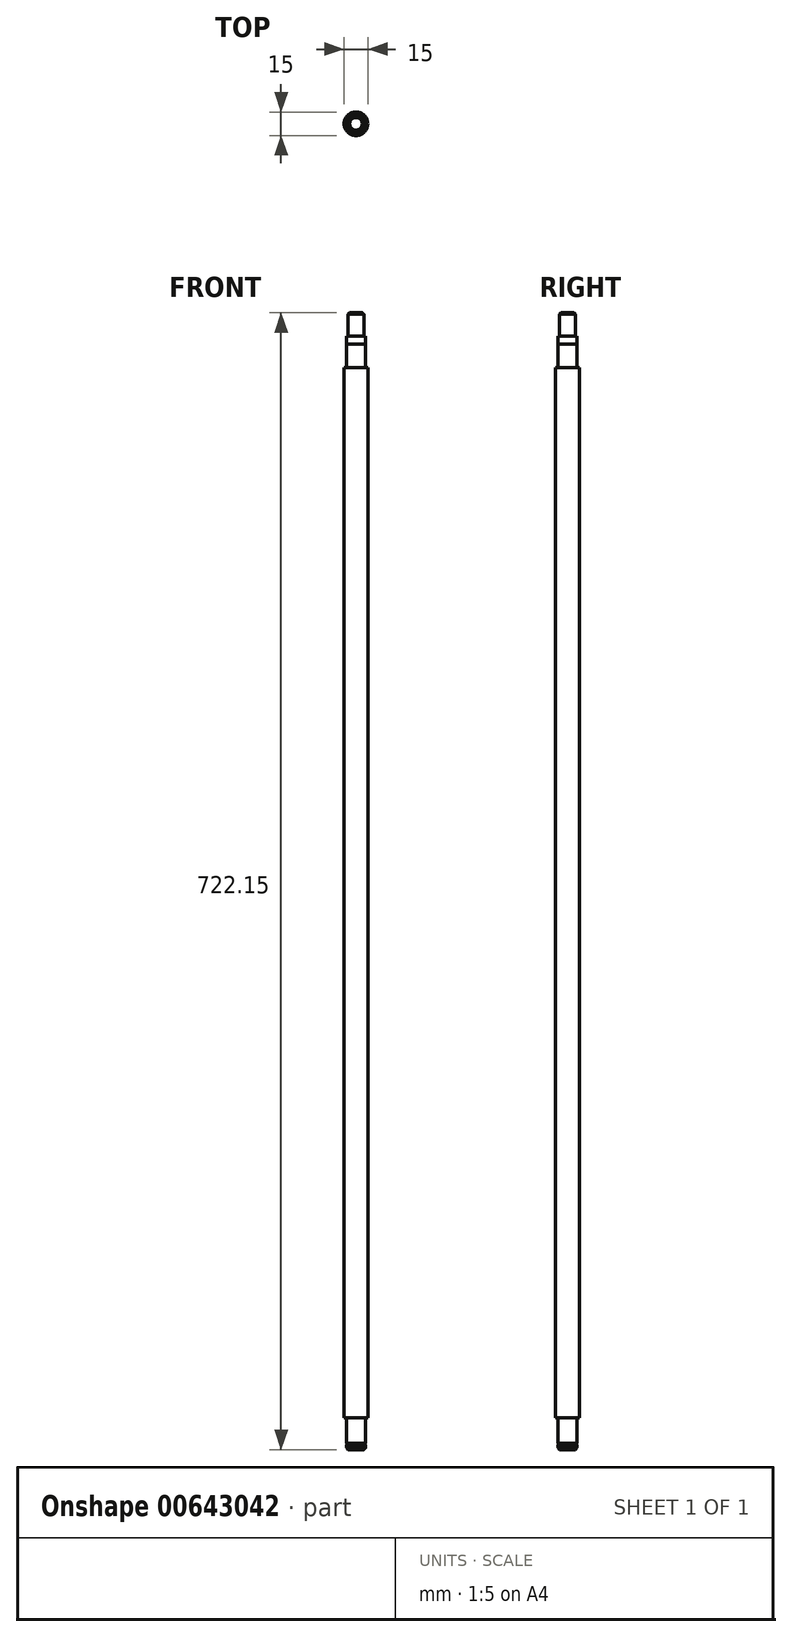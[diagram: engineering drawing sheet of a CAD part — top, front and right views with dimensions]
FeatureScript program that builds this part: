
annotation { "Feature Type Name" : "Feature", "Feature Type Description" : "" }
export const myFeature = defineFeature(function(context is Context, id is Id, definition is map)
    precondition{}
    {
        {
            var Q0;
            Q0=qCreatedBy(makeId("Top.planeOp"),FACE);
            var sketch = newSketch(context, id + "F0", { "sketchPlane" : qUnion([Q0])});
            skCircle(sketch, "E0", {"center": v(0, 0) * mm, "radius": 6 * mm});
            skSolve(sketch);
        }
        {
            var Q0;
            Q0=makeQuery(id+"F0.imprint","IMPRINT",FACE,{"disambiguationData":[TD([[makeQuery(id+"F0.imprint","IMPRINT",EDGE,{"derivedFrom":sQuery(id+"F0.wireOp",EDGE,"E0")}),1.0]])]});
            extrude(context, id + "F1", {"entities" : qUnion([Q0]), "depth" : 3 * mm});
        }
        {
            var Q0;
            Q0=makeQuery(id+"F1.opExtrude","CAP_FACE",FACE,{"disambiguationData":[OSD([sQuery(id+"F0.wireOp",EDGE,"E0")])],"isStart":false});
            var sketch = newSketch(context, id + "F2", { "sketchPlane" : qUnion([Q0])});
            skCircle(sketch, "E1", {"center": v(0, 0) * mm, "radius": 5.75 * mm});
            skSolve(sketch);
        }
        {
            var Q0;
            Q0=makeQuery(id+"F2.imprint","IMPRINT",FACE,{"disambiguationData":[TD([[makeQuery(id+"F2.imprint","IMPRINT",EDGE,{"derivedFrom":sQuery(id+"F2.wireOp",EDGE,"E1")}),1.0]])]});
            extrude(context, id + "F3", {"entities" : qUnion([Q0]), "operationType" : NewBodyOperationType.ADD, "depth" : 1.15 * mm});
        }
        {
            var Q0;
            Q0=makeQuery(id+"F3.opExtrude","CAP_FACE",FACE,{"disambiguationData":[OSD([sQuery(id+"F2.wireOp",EDGE,"E1")])],"isStart":false});
            var sketch = newSketch(context, id + "F4", { "sketchPlane" : qUnion([Q0])});
            skCircle(sketch, "E2", {"center": v(0, 0) * mm, "radius": 6 * mm});
            skSolve(sketch);
        }
        {
            var Q0;
            Q0=makeQuery(id+"F4.imprint","IMPRINT",FACE,{"disambiguationData":[TD([[makeQuery(id+"F4.imprint","IMPRINT",EDGE,{"derivedFrom":sQuery(id+"F4.wireOp",EDGE,"E2")}),1.0]])]});
            var Q1;
            Q1=makeQuery(id+"F4.imprint","IMPRINT",FACE,{"disambiguationData":[TD([[makeQuery(id+"F4.imprint","IMPRINT",EDGE,{"derivedFrom":makeQuery(id+"F3.opExtrude","CAP_EDGE",EDGE,{"disambiguationData":[OSD([sQuery(id+"F2.wireOp",EDGE,"E1")])],"isStart":false})}),1.0]])]});
            extrude(context, id + "F5", {"entities" : qUnion([Q0, Q1]), "operationType" : NewBodyOperationType.ADD, "depth" : 16 * mm});
        }
        {
            var Q0;
            Q0=makeQuery(id+"F5.opExtrude","CAP_FACE",FACE,{"disambiguationData":[OSD([sQuery(id+"F4.wireOp",EDGE,"E2")])],"isStart":false});
            var sketch = newSketch(context, id + "F6", { "sketchPlane" : qUnion([Q0])});
            skCircle(sketch, "E3", {"center": v(0, 0) * mm, "radius": 7.5 * mm});
            skSolve(sketch);
        }
        {
            var Q0;
            Q0=makeQuery(id+"F6.imprint","IMPRINT",FACE,{"disambiguationData":[TD([[makeQuery(id+"F6.imprint","IMPRINT",EDGE,{"derivedFrom":makeQuery(id+"F5.opExtrude","CAP_EDGE",EDGE,{"disambiguationData":[OSD([sQuery(id+"F4.wireOp",EDGE,"E2")])],"isStart":false})}),1.0]])]});
            var Q1;
            Q1=makeQuery(id+"F6.imprint","IMPRINT",FACE,{"disambiguationData":[TD([[makeQuery(id+"F6.imprint","IMPRINT",EDGE,{"derivedFrom":sQuery(id+"F6.wireOp",EDGE,"E3")}),1.0]])]});
            extrude(context, id + "F7", {"entities" : qUnion([Q0, Q1]), "operationType" : NewBodyOperationType.ADD, "depth" : 667 * mm});
        }
        {
            var Q0;
            Q0=makeQuery(id+"F7.opExtrude","CAP_FACE",FACE,{"disambiguationData":[OSD([sQuery(id+"F6.wireOp",EDGE,"E3")])],"isStart":false});
            var sketch = newSketch(context, id + "F8", { "sketchPlane" : qUnion([Q0])});
            skCircle(sketch, "E4", {"center": v(0, 0) * mm, "radius": 6 * mm});
            skSolve(sketch);
        }
        {
            var Q0;
            Q0=makeQuery(id+"F8.imprint","IMPRINT",FACE,{"disambiguationData":[TD([[makeQuery(id+"F8.imprint","IMPRINT",EDGE,{"derivedFrom":sQuery(id+"F8.wireOp",EDGE,"E4")}),1.0]])]});
            extrude(context, id + "F9", {"entities" : qUnion([Q0]), "operationType" : NewBodyOperationType.ADD, "depth" : 15 * mm, "offsetDistance" : 25 * mm});
        }
        {
            var Q0;
            Q0=makeQuery(id+"F9.opExtrude","CAP_FACE",FACE,{"disambiguationData":[OSD([sQuery(id+"F8.wireOp",EDGE,"E4")])],"isStart":false});
            var sketch = newSketch(context, id + "F10", { "sketchPlane" : qUnion([Q0])});
            skCircle(sketch, "E5", {"center": v(0, 0) * mm, "radius": 5.95 * mm});
            skSolve(sketch);
        }
        {
            var Q0;
            Q0=makeQuery(id+"F10.imprint","IMPRINT",FACE,{"disambiguationData":[TD([[makeQuery(id+"F10.imprint","IMPRINT",EDGE,{"derivedFrom":sQuery(id+"F10.wireOp",EDGE,"E5")}),1.0]])]});
            extrude(context, id + "F11", {"entities" : qUnion([Q0]), "operationType" : NewBodyOperationType.ADD, "depth" : 2 * mm, "offsetDistance" : 25 * mm});
        }
        {
            var Q0;
            Q0=makeQuery(id+"F11.opExtrude","CAP_FACE",FACE,{"disambiguationData":[OSD([sQuery(id+"F10.wireOp",EDGE,"E5")])],"isStart":false});
            var sketch = newSketch(context, id + "F12", { "sketchPlane" : qUnion([Q0])});
            skCircle(sketch, "E6", {"center": v(0, 0) * mm, "radius": 5.95 * mm});
            skSolve(sketch);
        }
        {
            var Q0;
            Q0=makeQuery(id+"F12.imprint","IMPRINT",FACE,{"disambiguationData":[TD([[makeQuery(id+"F12.imprint","IMPRINT",EDGE,{"derivedFrom":makeQuery(id+"F11.opExtrude","CAP_EDGE",EDGE,{"disambiguationData":[OSD([sQuery(id+"F10.wireOp",EDGE,"E5")])],"isStart":false})}),1.0]])]});
            var Q1;
            Q1=makeQuery(id+"F12.imprint","IMPRINT",FACE,{"disambiguationData":[TD([[makeQuery(id+"F12.imprint","IMPRINT",EDGE,{"derivedFrom":sQuery(id+"F12.wireOp",EDGE,"E6")}),1.0]])]});
            extrude(context, id + "F13", {"entities" : qUnion([Q0, Q1]), "operationType" : NewBodyOperationType.ADD, "depth" : 3 * mm, "offsetDistance" : 25 * mm});
        }
        {
            var Q0;
            Q0=makeQuery(id+"F13.opExtrude","CAP_FACE",FACE,{"disambiguationData":[OSD([sQuery(id+"F12.wireOp",EDGE,"E6")])],"isStart":false});
            var sketch = newSketch(context, id + "F14", { "sketchPlane" : qUnion([Q0])});
            skCircle(sketch, "E7", {"center": v(0, 0) * mm, "radius": 5 * mm});
            skSolve(sketch);
        }
        {
            var Q0;
            Q0=makeQuery(id+"F14.imprint","IMPRINT",FACE,{"disambiguationData":[TD([[makeQuery(id+"F14.imprint","IMPRINT",EDGE,{"derivedFrom":sQuery(id+"F14.wireOp",EDGE,"E7")}),1.0]])]});
            extrude(context, id + "F15", {"entities" : qUnion([Q0]), "operationType" : NewBodyOperationType.ADD, "depth" : 15 * mm, "offsetDistance" : 25 * mm});
        }
        {
            var Q0;
            Q0=makeQuery(id+"F15.opExtrude","CAP_EDGE",EDGE,{"disambiguationData":[OSD([sQuery(id+"F14.wireOp",EDGE,"E7")])],"isStart":false});
            var Q1;
            Q1=makeQuery(id+"F1.opExtrude","CAP_EDGE",EDGE,{"disambiguationData":[OSD([sQuery(id+"F0.wireOp",EDGE,"E0")])],"isStart":true});
            chamfer(context, id + "F16", {"entities" : qUnion([Q0, Q1]), "width" : 1 * mm, "tangentPropagation" : true});
        }
    });
